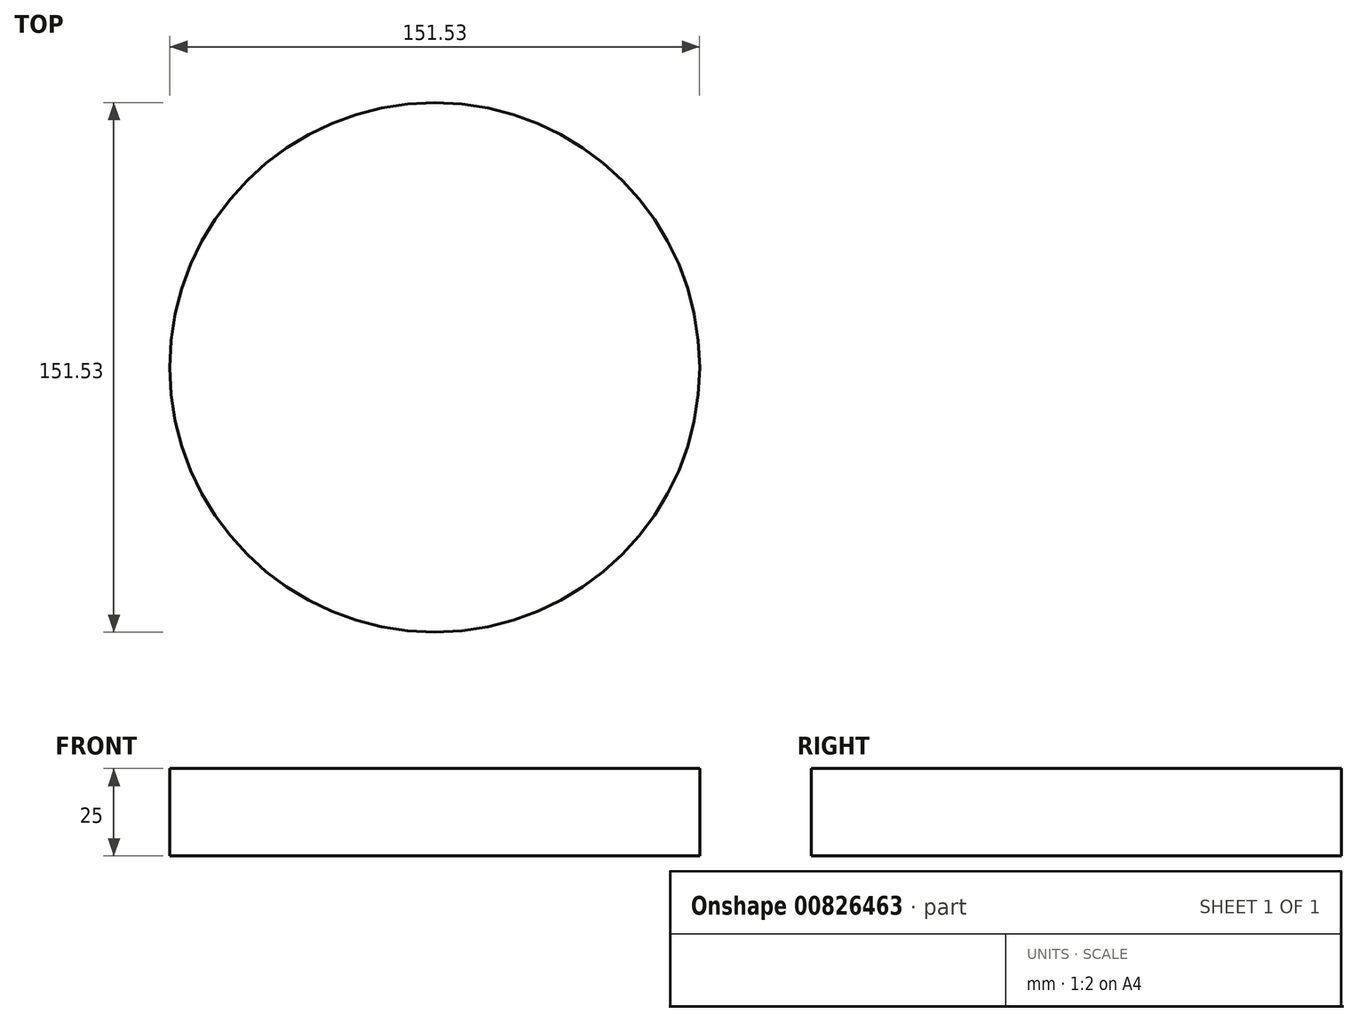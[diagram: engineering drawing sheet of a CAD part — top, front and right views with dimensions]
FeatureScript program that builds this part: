
annotation { "Feature Type Name" : "Feature", "Feature Type Description" : "" }
export const myFeature = defineFeature(function(context is Context, id is Id, definition is map)
    precondition{}
    {
        {
            var Q0;
            Q0=qCreatedBy(makeId("Top.planeOp"),FACE);
            var sketch = newSketch(context, id + "F0", { "sketchPlane" : qUnion([Q0])});
            skCircle(sketch, "E0", {"center": v(-6.04, -23.94) * mm, "radius": 75.77 * mm});
            skSolve(sketch);
        }
        {
            var Q0;
            Q0 = qSketchRegion(id + "F0", true);
            var Q1;
            Q1=makeQuery(id+"F0.imprint","IMPRINT",FACE,{"disambiguationData":[TD([[makeQuery(id+"F0.imprint","IMPRINT",EDGE,{"derivedFrom":sQuery(id+"F0.wireOp",EDGE,"e5f8776a-cf91-4b3a-9aca-ffc1af4f3cde")}),1.0]])]});
            extrude(context, id + "F1", {"entities" : qUnion([Q0, Q1]), "depth" : 25 * mm, "offsetDistance" : 25 * mm});
        }
    });
